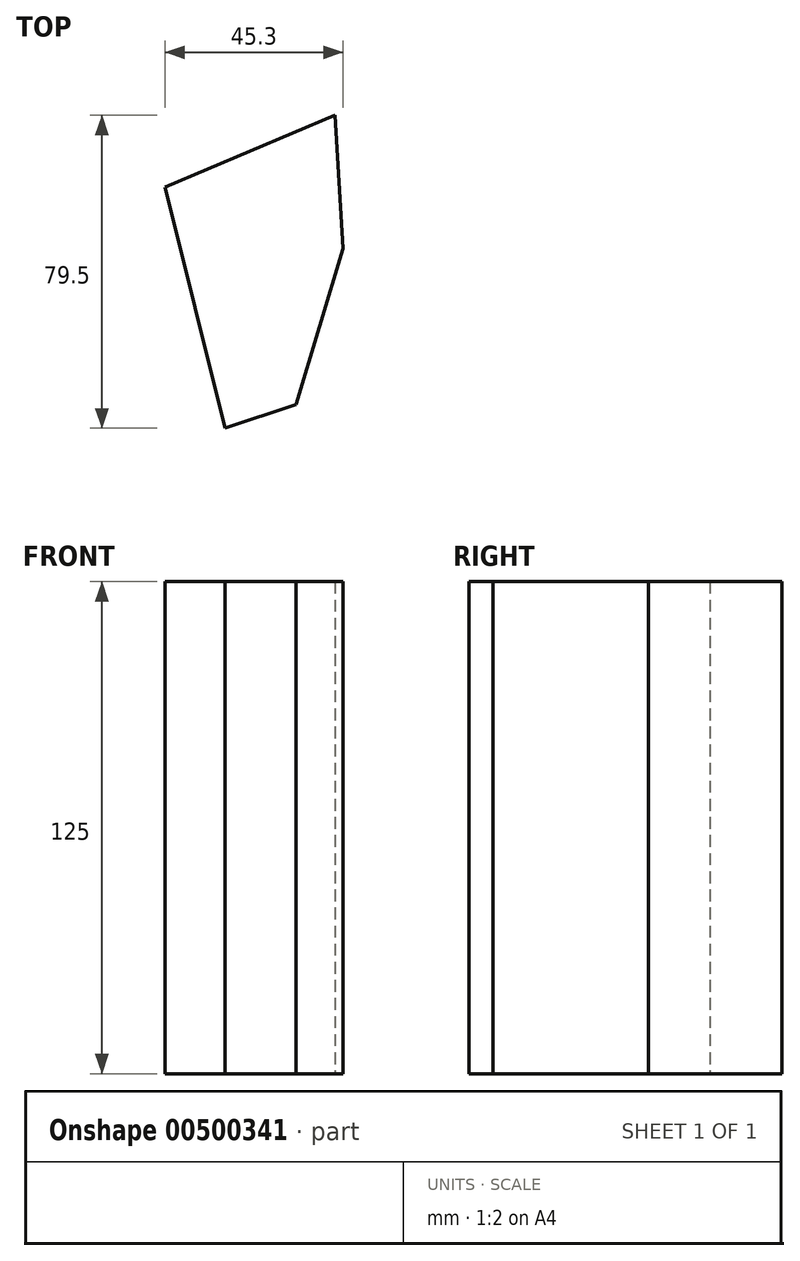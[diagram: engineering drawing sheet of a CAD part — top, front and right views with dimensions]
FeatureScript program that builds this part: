
annotation { "Feature Type Name" : "Feature", "Feature Type Description" : "" }
export const myFeature = defineFeature(function(context is Context, id is Id, definition is map)
    precondition{}
    {
        {
            var Q0;
            Q0=qCreatedBy(makeId("Top.planeOp"),FACE);
            var sketch = newSketch(context, id + "F0", { "sketchPlane" : qUnion([Q0])});
            skLineSegment(sketch, "E0", {"start": v(-25.5, -30.75) * mm, "end": v(-40.8, 30.45) * mm});
            skLineSegment(sketch, "E1", {"start": v(-40.8, 30.45) * mm, "end": v(2.4, 48.75) * mm});
            skLineSegment(sketch, "E2", {"start": v(2.4, 48.75) * mm, "end": v(4.5, 14.85) * mm});
            skLineSegment(sketch, "E3", {"start": v(4.5, 14.85) * mm, "end": v(-7.5, -24.75) * mm});
            skLineSegment(sketch, "E4", {"start": v(-7.5, -24.75) * mm, "end": v(-25.5, -30.75) * mm});
            skSolve(sketch);
        }
        {
            var Q0;
            Q0=makeQuery(id+"F0.imprint","IMPRINT",FACE,{"disambiguationData":[TD([[makeQuery(id+"F0.imprint","IMPRINT",EDGE,{"derivedFrom":sQuery(id+"F0.wireOp",EDGE,"E0")}),-1.0]])]});
            extrude(context, id + "F1", {"entities" : qUnion([Q0]), "depth" : 125 * mm});
        }
    });
